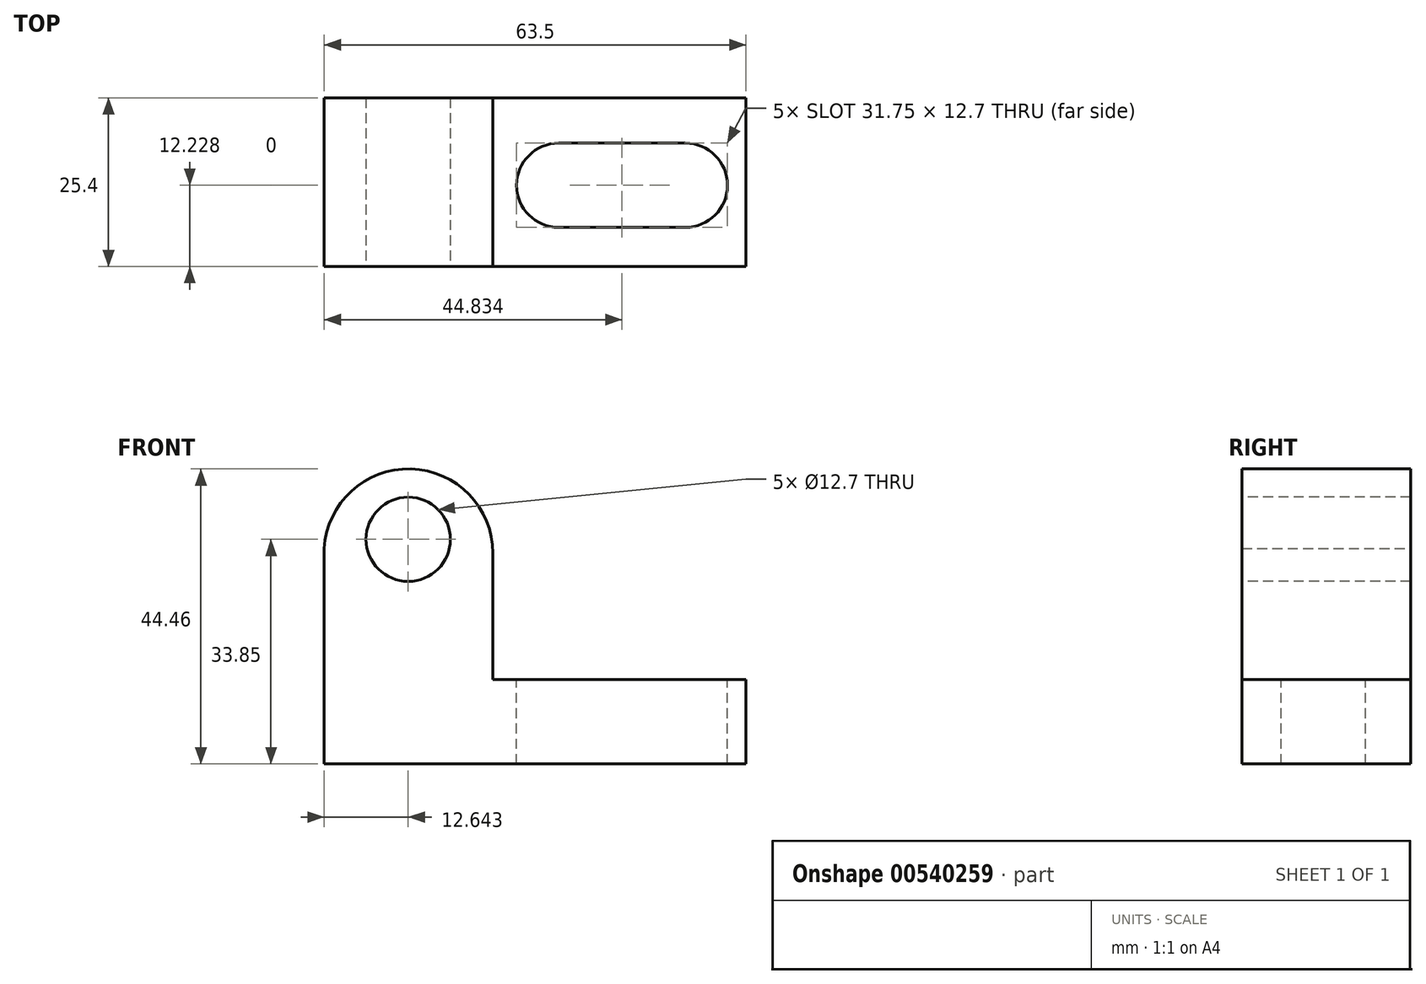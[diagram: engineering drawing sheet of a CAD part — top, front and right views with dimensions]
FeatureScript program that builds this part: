
annotation { "Feature Type Name" : "Feature", "Feature Type Description" : "" }
export const myFeature = defineFeature(function(context is Context, id is Id, definition is map)
    precondition{}
    {
        {
            var Q0;
            Q0=qCreatedBy(makeId("Front.planeOp"),FACE);
            var sketch = newSketch(context, id + "F0", { "sketchPlane" : qUnion([Q0])});
            skLineSegment(sketch, "E0", {"start": v(-81.54, 32.45) * mm, "end": v(-81.54, 0) * mm});
            skLineSegment(sketch, "E1", {"start": v(-81.54, 0) * mm, "end": v(-18.04, 0) * mm});
            skLineSegment(sketch, "E2", {"start": v(-18.04, 0) * mm, "end": v(-18.04, 12.7) * mm});
            skLineSegment(sketch, "E3", {"start": v(-18.04, 12.7) * mm, "end": v(-56.14, 12.7) * mm});
            skLineSegment(sketch, "E4", {"start": v(-56.14, 12.7) * mm, "end": v(-56.14, 31.75) * mm});
            skArc(sketch, "E5", {"start": v(-56.14, 31.75) * mm, "mid": v(-68.5, 44.45) * mm, "end": v(-81.54, 32.45) * mm});
            skSolve(sketch);
        }
        {
            var Q0;
            Q0=makeQuery(id+"F0.imprint","IMPRINT",FACE,{"disambiguationData":[TD([[makeQuery(id+"F0.imprint","IMPRINT",EDGE,{"derivedFrom":sQuery(id+"F0.wireOp",EDGE,"E0")}),1.0]])]});
            extrude(context, id + "F1", {"entities" : qUnion([Q0]), "depth" : 25.4 * mm, "offsetDistance" : 25.4 * mm});
        }
        {
            var Q0;
            Q0=makeQuery(id+"F1.opExtrude","CAP_FACE",FACE,{"disambiguationData":[OSD([sQuery(id+"F0.wireOp",EDGE,"E0"),sQuery(id+"F0.wireOp",EDGE,"E1"),sQuery(id+"F0.wireOp",EDGE,"E2"),sQuery(id+"F0.wireOp",EDGE,"E3"),sQuery(id+"F0.wireOp",EDGE,"E4"),sQuery(id+"F0.wireOp",EDGE,"E5")])],"isStart":false});
            var sketch = newSketch(context, id + "F2", { "sketchPlane" : qUnion([Q0])});
            skCircle(sketch, "E6", {"center": v(-68.9, 33.85) * mm, "radius": 6.35 * mm});
            skSolve(sketch);
        }
        {
            var Q0;
            Q0=makeQuery(id+"F2.imprint","IMPRINT",FACE,{"disambiguationData":[TD([[makeQuery(id+"F2.imprint","IMPRINT",EDGE,{"derivedFrom":sQuery(id+"F2.wireOp",EDGE,"E6")}),1.0]])]});
            extrude(context, id + "F3", {"entities" : qUnion([Q0]), "operationType" : NewBodyOperationType.REMOVE, "endBound" : BoundingType.THROUGH_ALL, "oppositeDirection" : true, "depth" : 25.4 * mm, "offsetDistance" : 25.4 * mm});
        }
        {
            var Q0;
            Q0=makeQuery(id+"F1.opExtrude","SWEPT_FACE",FACE,{"disambiguationData":[OSD([sQuery(id+"F0.wireOp",EDGE,"E3")])]});
            var sketch = newSketch(context, id + "F4", { "sketchPlane" : qUnion([Q0])});
            skLineSegment(sketch, "E7", {"start": v(-46.23, -6.82) * mm, "end": v(-46.23, -19.52) * mm});
            skLineSegment(sketch, "E8", {"start": v(-46.23, -19.52) * mm, "end": v(-27.18, -19.52) * mm});
            skLineSegment(sketch, "E9", {"start": v(-27.18, -19.52) * mm, "end": v(-27.18, -6.82) * mm});
            skLineSegment(sketch, "E10", {"start": v(-27.18, -6.82) * mm, "end": v(-46.23, -6.82) * mm});
            skSolve(sketch);
        }
        {
            var Q0;
            Q0=makeQuery(id+"F4.imprint","IMPRINT",FACE,{"disambiguationData":[TD([[makeQuery(id+"F4.imprint","IMPRINT",EDGE,{"derivedFrom":sQuery(id+"F4.wireOp",EDGE,"E7")}),1.0]])]});
            extrude(context, id + "F5", {"entities" : qUnion([Q0]), "operationType" : NewBodyOperationType.REMOVE, "endBound" : BoundingType.THROUGH_ALL, "oppositeDirection" : true, "depth" : 25.4 * mm, "offsetDistance" : 25.4 * mm});
        }
        {
            var Q0;
            Q0=makeQuery(id+"F1.opExtrude","SWEPT_FACE",FACE,{"disambiguationData":[OSD([sQuery(id+"F0.wireOp",EDGE,"E3")])]});
            var sketch = newSketch(context, id + "F6", { "sketchPlane" : qUnion([Q0])});
            skArc(sketch, "E11", {"start": v(-46.23, -6.82) * mm, "mid": v(-52.58, -13.17) * mm, "end": v(-46.23, -19.52) * mm});
            skArc(sketch, "E12", {"start": v(-27.18, -19.52) * mm, "mid": v(-20.83, -13.17) * mm, "end": v(-27.18, -6.82) * mm});
            skSolve(sketch);
        }
        {
            var Q0;
            Q0=makeQuery(id+"F6.imprint","IMPRINT",FACE,{"disambiguationData":[TD([[makeQuery(id+"F6.imprint","IMPRINT",EDGE,{"derivedFrom":sQuery(id+"F6.wireOp",EDGE,"E11")}),1.0]])]});
            extrude(context, id + "F7", {"entities" : qUnion([Q0]), "operationType" : NewBodyOperationType.REMOVE, "endBound" : BoundingType.THROUGH_ALL, "oppositeDirection" : true, "depth" : 25.4 * mm, "offsetDistance" : 25.4 * mm});
        }
        {
            var Q0;
            Q0=makeQuery(id+"F1.opExtrude","SWEPT_FACE",FACE,{"disambiguationData":[OSD([sQuery(id+"F0.wireOp",EDGE,"E3")])]});
            var sketch = newSketch(context, id + "F8", { "sketchPlane" : qUnion([Q0])});
            skArc(sketch, "E13", {"start": v(-27.18, -19.52) * mm, "mid": v(-20.83, -13.17) * mm, "end": v(-27.18, -6.82) * mm});
            skSolve(sketch);
        }
        {
            var Q0;
            Q0=makeQuery(id+"F8.imprint","IMPRINT",FACE,{"disambiguationData":[TD([[makeQuery(id+"F8.imprint","IMPRINT",EDGE,{"derivedFrom":sQuery(id+"F8.wireOp",EDGE,"E13")}),1.0]])]});
            extrude(context, id + "F9", {"entities" : qUnion([Q0]), "operationType" : NewBodyOperationType.REMOVE, "endBound" : BoundingType.THROUGH_ALL, "oppositeDirection" : true, "depth" : 25.4 * mm, "offsetDistance" : 25.4 * mm});
        }
    });
